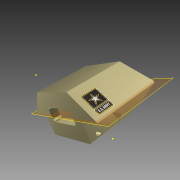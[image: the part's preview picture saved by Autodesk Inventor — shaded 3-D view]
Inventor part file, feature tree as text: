
AUTODESK INVENTOR PART (.ipt)
format: ipt  version: 2015 (Build 190159000, 159)  size: 867,840 bytes
history: native  units: in
note: dims shown in document units (in); Inventor stores cm internally (conversion verified against a paired STEP export)
features: sketch x13, extrude x9, chamfer x4, plane x4, mirror x2, fillet x1, other x1, projected_geometry x1
ambient origin geometry x8: Origin, YZ Plane, XZ Plane, XY Plane, X Axis, Y Axis, Z Axis, Center Point
bodies: Solid1 (feature_tree)
feature tree (35):
  extrude  "Extrusion1"  Depth=4.0in
  chamfer  "Chamfer1"  Distance=6.75in
  chamfer  "Chamfer2"  Distance=1.625in Angle=45.0deg
  chamfer  "Chamfer3"  Distance=1.435in Angle=45.0deg
  chamfer  "Chamfer4"  Distance=1.625in Angle=45.0deg
  plane  "Work Plane1"
  plane  "Work Plane2"
  extrude  "Extrusion2"  [1 undecoded]
  extrude  "Extrusion3"  Depth=0.759in
  mirror  "Mirror1"
  plane  "Work Plane3"
  extrude  "Extrusion4"  Depth=1.38in TaperAngle=0.0deg
  mirror  "Mirror2"
  sketch  "Sketch5"  dims[d23=1.5315in d24=0.25in d25=0.36in]
  extrude  "Extrusion5"  Depth=0.25in
  fillet  "Fillet1"  Radius=0.36in
  plane  "Work Plane4"
  extrude  "Extrusion6"  Depth=2.5in
  extrude  "Extrusion7"  Depth=0.745in
  sketch  "Sketch9"  dims[d50=0.2in d51=0.05in d52=0.0in]
  sketch  "Sketch10"  dims[d53=0.1in d54=0.0in]
  sketch  "Sketch11"  dims[d55=0.1in d56=0.0in]
  extrude  "Extrusion8"  Depth=0.57in TaperAngle=0.0deg
  extrude  "Extrusion9"  Depth=0.05in TaperAngle=0.0deg
  sketch  "Sketch1"  dims[d0=3.06in d1=4.0in d2=6.75in d3=0.0in d4=1.625in d5=0.125in d6=45.0deg d7=1.435in d8=0.125in d9=45.0deg d10=1.625in d11=0.125in d12=45.0deg]
  sketch  "Sketch2"  dims[d13=1.435in d14=0.125in d15=45.0deg d16=-1.38in]
  sketch  "Sketch3"  dims[d17=1.375in d18=0.759in]
  sketch  "Sketch4"  dims[d19=1.38in d20=0.0in d21=1.38in d22=0.0in]
  other  "Image1"
  sketch  "Sketch6"  dims[d26=0.4in d27=0.0in d44=2.5in]
  sketch  "Sketch7"  dims[d45=1.0in d46=0.745in]
  sketch  "Sketch8"  dims[d47=1.03in d48=0.57in d49=0.0in]
  sketch  "Sketch12"  dims[d57=0.05in d58=0.0in]
  projected_geometry  "Projected Loop1"
  sketch  "Sketch13"
note: 1 required parameter value undecoded (feature->parameter linkage not recoverable at this tier; creation-order binding heuristic only, values carry confidence <= 0.55)
